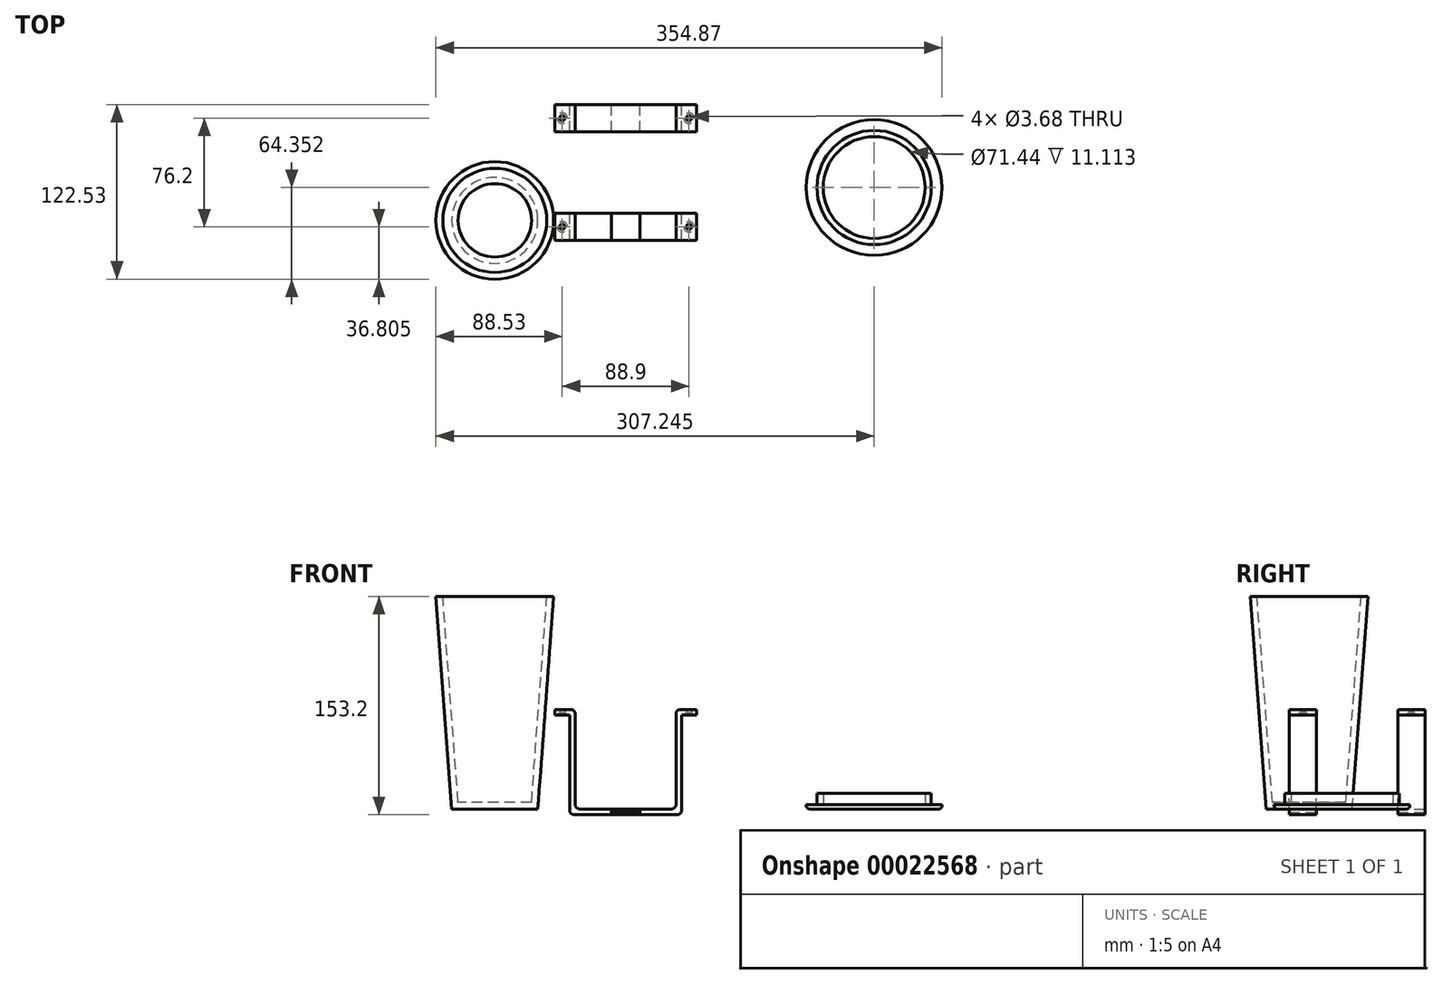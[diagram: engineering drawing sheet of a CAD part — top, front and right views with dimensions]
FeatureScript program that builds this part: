
annotation { "Feature Type Name" : "Feature", "Feature Type Description" : "" }
export const myFeature = defineFeature(function(context is Context, id is Id, definition is map)
    precondition{}
    {
        {
            var Q0;
            Q0=qCreatedBy(makeId("Front.planeOp"),FACE);
            var sketch = newSketch(context, id + "F0", { "sketchPlane" : qUnion([Q0])});
            skLineSegment(sketch, "E0", {"start": v(32.15, 0) * mm, "end": v(-32.15, 0) * mm});
            skLineSegment(sketch, "E1", {"start": v(35.32, 3.18) * mm, "end": v(35.32, 66.68) * mm});
            skLineSegment(sketch, "E2", {"start": v(-35.32, 3.18) * mm, "end": v(-35.32, 66.68) * mm});
            skLineSegment(sketch, "E3", {"start": v(-38.5, 69.85) * mm, "end": v(-49.6, 69.85) * mm});
            skLineSegment(sketch, "E4", {"start": v(38.5, 69.85) * mm, "end": v(49.6, 69.85) * mm});
            skLineSegment(sketch, "E5.0", {"start": v(39.3, 65.88) * mm, "end": v(49.6, 65.88) * mm});
            skLineSegment(sketch, "E5.1", {"start": v(-39.3, 65.88) * mm, "end": v(-49.6, 65.88) * mm});
            skLineSegment(sketch, "E5.2", {"start": v(-39.3, -0.8) * mm, "end": v(-39.3, 65.88) * mm});
            skLineSegment(sketch, "E5.3", {"start": v(36.12, -3.97) * mm, "end": v(-36.12, -3.97) * mm});
            skLineSegment(sketch, "E5.4", {"start": v(39.3, -0.8) * mm, "end": v(39.3, 65.88) * mm});
            skLineSegment(sketch, "E6", {"start": v(49.6, 69.85) * mm, "end": v(49.6, 65.88) * mm});
            skLineSegment(sketch, "E7", {"start": v(-49.6, 69.85) * mm, "end": v(-49.6, 65.88) * mm});
            skPoint(sketch, "E8.visualSharp", {"position": v(-35.32, 69.85) * mm});
            skArc(sketch, "E8.filletArc", {"start": v(-35.32, 66.68) * mm, "mid": v(-36.25, 68.92) * mm, "end": v(-38.5, 69.85) * mm});
            skPoint(sketch, "E9.visualSharp", {"position": v(-35.32, 0) * mm});
            skArc(sketch, "E9.filletArc", {"start": v(-35.32, 3.18) * mm, "mid": v(-34.4, 0.93) * mm, "end": v(-32.15, 0) * mm});
            skPoint(sketch, "E10.visualSharp", {"position": v(-39.3, -3.97) * mm});
            skArc(sketch, "E10.filletArc", {"start": v(-39.3, -0.8) * mm, "mid": v(-38.36, -3.04) * mm, "end": v(-36.12, -3.97) * mm});
            skPoint(sketch, "E11.visualSharp", {"position": v(39.3, -3.97) * mm});
            skArc(sketch, "E11.filletArc", {"start": v(36.12, -3.97) * mm, "mid": v(38.36, -3.04) * mm, "end": v(39.3, -0.8) * mm});
            skPoint(sketch, "E12.visualSharp", {"position": v(35.32, 0) * mm});
            skArc(sketch, "E12.filletArc", {"start": v(32.15, 0) * mm, "mid": v(34.4, 0.93) * mm, "end": v(35.32, 3.18) * mm});
            skPoint(sketch, "E13.visualSharp", {"position": v(35.32, 69.85) * mm});
            skArc(sketch, "E13.filletArc", {"start": v(38.5, 69.85) * mm, "mid": v(36.25, 68.92) * mm, "end": v(35.32, 66.68) * mm});
            skSolve(sketch);
        }
        {
            var Q0;
            Q0 = qSketchRegion(id + "F0", true);
            extrude(context, id + "F1", {"entities" : qUnion([Q0]), "depth" : 19.05 * mm});
        }
        {
            var Q0;
            Q0=makeQuery(id+"F1.opExtrude","SWEPT_BODY",BODY,{"disambiguationData":[OSD([sQuery(id+"F0.wireOp",EDGE,"E0"),sQuery(id+"F0.wireOp",EDGE,"E1"),sQuery(id+"F0.wireOp",EDGE,"E2"),sQuery(id+"F0.wireOp",EDGE,"E3"),sQuery(id+"F0.wireOp",EDGE,"E4"),sQuery(id+"F0.wireOp",EDGE,"E5.0"),sQuery(id+"F0.wireOp",EDGE,"E5.1"),sQuery(id+"F0.wireOp",EDGE,"E5.2"),sQuery(id+"F0.wireOp",EDGE,"E5.3"),sQuery(id+"F0.wireOp",EDGE,"E5.4"),sQuery(id+"F0.wireOp",EDGE,"E8.filletArc"),sQuery(id+"F0.wireOp",EDGE,"E9.filletArc"),sQuery(id+"F0.wireOp",EDGE,"E10.filletArc"),sQuery(id+"F0.wireOp",EDGE,"E11.filletArc"),sQuery(id+"F0.wireOp",EDGE,"E12.filletArc"),sQuery(id+"F0.wireOp",EDGE,"E13.filletArc"),sQuery(id+"F0.wireOp",EDGE,"E6"),sQuery(id+"F0.wireOp",EDGE,"E7")])]});
            transform(context, id + "F2", {"entities" : qUnion([Q0]), "transformType" : TransformType.TRANSLATION_3D, "dx" : 0 * mm, "dy" : 76.2 * mm, "dz" : 0 * mm, "makeCopy" : true});
        }
        {
            var Q0;
            Q0=makeQuery(id+"F1.opExtrude","CAP_FACE",FACE,{"disambiguationData":[OSD([sQuery(id+"F0.wireOp",EDGE,"E0"),sQuery(id+"F0.wireOp",EDGE,"E1"),sQuery(id+"F0.wireOp",EDGE,"E2"),sQuery(id+"F0.wireOp",EDGE,"E3"),sQuery(id+"F0.wireOp",EDGE,"E4"),sQuery(id+"F0.wireOp",EDGE,"E5.0"),sQuery(id+"F0.wireOp",EDGE,"E5.1"),sQuery(id+"F0.wireOp",EDGE,"E5.2"),sQuery(id+"F0.wireOp",EDGE,"E5.3"),sQuery(id+"F0.wireOp",EDGE,"E5.4"),sQuery(id+"F0.wireOp",EDGE,"E8.filletArc"),sQuery(id+"F0.wireOp",EDGE,"E9.filletArc"),sQuery(id+"F0.wireOp",EDGE,"E10.filletArc"),sQuery(id+"F0.wireOp",EDGE,"E11.filletArc"),sQuery(id+"F0.wireOp",EDGE,"E12.filletArc"),sQuery(id+"F0.wireOp",EDGE,"E13.filletArc"),sQuery(id+"F0.wireOp",EDGE,"E6"),sQuery(id+"F0.wireOp",EDGE,"E7")])],"isStart":false});
            var sketch = newSketch(context, id + "F3", { "sketchPlane" : qUnion([Q0])});
            skLineSegment(sketch, "E14", {"start": v(0, 0) * mm, "end": v(0, -3.97) * mm, "construction": true});
            skLineSegment(sketch, "E15.bottom", {"start": v(-9.92, 0) * mm, "end": v(0, 0) * mm});
            skLineSegment(sketch, "E15.top", {"start": v(-9.92, -2.5) * mm, "end": v(9.92, -2.5) * mm});
            skLineSegment(sketch, "E15.left", {"start": v(-9.92, 0) * mm, "end": v(-9.92, -2.5) * mm});
            skLineSegment(sketch, "E15.right", {"start": v(9.92, 0) * mm, "end": v(9.92, -2.5) * mm});
            skLineSegment(sketch, "E16", {"start": v(0, 0) * mm, "end": v(9.92, 0) * mm});
            skSolve(sketch);
        }
        {
            var Q0;
            Q0 = qSketchRegion(id + "F3", true);
            extrude(context, id + "F4", {"entities" : qUnion([Q0]), "operationType" : NewBodyOperationType.REMOVE, "endBound" : BoundingType.UP_TO_NEXT, "oppositeDirection" : true, "depth" : 25.4 * mm});
        }
        {
            var Q0;
            Q0=makeQuery(id+"F2.opPattern","COPY",FACE,{"derivedFrom":makeQuery(id+"F1.opExtrude","CAP_FACE",FACE,{"disambiguationData":[OSD([sQuery(id+"F0.wireOp",EDGE,"E0"),sQuery(id+"F0.wireOp",EDGE,"E1"),sQuery(id+"F0.wireOp",EDGE,"E2"),sQuery(id+"F0.wireOp",EDGE,"E3"),sQuery(id+"F0.wireOp",EDGE,"E4"),sQuery(id+"F0.wireOp",EDGE,"E5.0"),sQuery(id+"F0.wireOp",EDGE,"E5.1"),sQuery(id+"F0.wireOp",EDGE,"E5.2"),sQuery(id+"F0.wireOp",EDGE,"E5.3"),sQuery(id+"F0.wireOp",EDGE,"E5.4"),sQuery(id+"F0.wireOp",EDGE,"E8.filletArc"),sQuery(id+"F0.wireOp",EDGE,"E9.filletArc"),sQuery(id+"F0.wireOp",EDGE,"E10.filletArc"),sQuery(id+"F0.wireOp",EDGE,"E11.filletArc"),sQuery(id+"F0.wireOp",EDGE,"E12.filletArc"),sQuery(id+"F0.wireOp",EDGE,"E13.filletArc"),sQuery(id+"F0.wireOp",EDGE,"E6"),sQuery(id+"F0.wireOp",EDGE,"E7")])],"isStart":true}),"instanceName":"1"});
            var sketch = newSketch(context, id + "F5", { "sketchPlane" : qUnion([Q0])});
            skLineSegment(sketch, "E17", {"start": v(0, 0) * mm, "end": v(0, -3.97) * mm});
            skLineSegment(sketch, "E18.bottom", {"start": v(-9.92, -2.25) * mm, "end": v(9.92, -2.25) * mm});
            skLineSegment(sketch, "E18.top", {"start": v(-9.92, -3.97) * mm, "end": v(9.92, -3.97) * mm});
            skLineSegment(sketch, "E18.left", {"start": v(-9.92, -2.25) * mm, "end": v(-9.92, -3.97) * mm});
            skLineSegment(sketch, "E18.right", {"start": v(9.92, -2.25) * mm, "end": v(9.92, -3.97) * mm});
            skSolve(sketch);
        }
        {
            var Q0;
            Q0 = qSketchRegion(id + "F5", true);
            extrude(context, id + "F6", {"entities" : qUnion([Q0]), "operationType" : NewBodyOperationType.REMOVE, "endBound" : BoundingType.UP_TO_NEXT, "oppositeDirection" : true, "depth" : 25.4 * mm});
        }
        {
            var Q0;
            Q0=makeQuery(id+"F2.opPattern","COPY",FACE,{"derivedFrom":makeQuery(id+"F1.opExtrude","SWEPT_FACE",FACE,{"disambiguationData":[OSD([sQuery(id+"F0.wireOp",EDGE,"E5.0")])]}),"instanceName":"1"});
            var sketch = newSketch(context, id + "F7", { "sketchPlane" : qUnion([Q0])});
            skLineSegment(sketch, "E19", {"start": v(44.45, -76.2) * mm, "end": v(44.45, -57.15) * mm, "construction": true});
            skLineSegment(sketch, "E20", {"start": v(44.45, 0) * mm, "end": v(44.45, 19.05) * mm, "construction": true});
            skLineSegment(sketch, "E21", {"start": v(-44.45, 19.05) * mm, "end": v(-44.45, 0) * mm, "construction": true});
            skLineSegment(sketch, "E22", {"start": v(-44.45, -57.15) * mm, "end": v(-44.45, -76.2) * mm, "construction": true});
            skPoint(sketch, "E23", {"position": v(44.45, -66.68) * mm});
            skPoint(sketch, "E24", {"position": v(-44.45, -66.68) * mm});
            skPoint(sketch, "E25", {"position": v(-44.45, 9.53) * mm});
            skPoint(sketch, "E26", {"position": v(44.45, 9.53) * mm});
            skSolve(sketch);
        }
        {
            var Q0;
            Q0=sQuery(id+"F7.wireOp",VERTEX,"E23");
            var Q1;
            Q1=sQuery(id+"F7.wireOp",VERTEX,"E24");
            var Q2;
            Q2=sQuery(id+"F7.wireOp",VERTEX,"E25");
            var Q3;
            Q3=sQuery(id+"F7.wireOp",VERTEX,"E26");
            var Q4;
            Q4=makeQuery(id+"F2.opPattern","COPY",BODY,{"derivedFrom":makeQuery(id+"F1.opExtrude","SWEPT_BODY",BODY,{"disambiguationData":[OSD([sQuery(id+"F0.wireOp",EDGE,"E0"),sQuery(id+"F0.wireOp",EDGE,"E1"),sQuery(id+"F0.wireOp",EDGE,"E2"),sQuery(id+"F0.wireOp",EDGE,"E3"),sQuery(id+"F0.wireOp",EDGE,"E4"),sQuery(id+"F0.wireOp",EDGE,"E5.0"),sQuery(id+"F0.wireOp",EDGE,"E5.1"),sQuery(id+"F0.wireOp",EDGE,"E5.2"),sQuery(id+"F0.wireOp",EDGE,"E5.3"),sQuery(id+"F0.wireOp",EDGE,"E5.4"),sQuery(id+"F0.wireOp",EDGE,"E8.filletArc"),sQuery(id+"F0.wireOp",EDGE,"E9.filletArc"),sQuery(id+"F0.wireOp",EDGE,"E10.filletArc"),sQuery(id+"F0.wireOp",EDGE,"E11.filletArc"),sQuery(id+"F0.wireOp",EDGE,"E12.filletArc"),sQuery(id+"F0.wireOp",EDGE,"E13.filletArc"),sQuery(id+"F0.wireOp",EDGE,"E6"),sQuery(id+"F0.wireOp",EDGE,"E7")])]}),"instanceName":"1"});
            var Q5;
            Q5=makeQuery(id+"F1.opExtrude","SWEPT_BODY",BODY,{"disambiguationData":[OSD([sQuery(id+"F0.wireOp",EDGE,"E0"),sQuery(id+"F0.wireOp",EDGE,"E1"),sQuery(id+"F0.wireOp",EDGE,"E2"),sQuery(id+"F0.wireOp",EDGE,"E3"),sQuery(id+"F0.wireOp",EDGE,"E4"),sQuery(id+"F0.wireOp",EDGE,"E5.0"),sQuery(id+"F0.wireOp",EDGE,"E5.1"),sQuery(id+"F0.wireOp",EDGE,"E5.2"),sQuery(id+"F0.wireOp",EDGE,"E5.3"),sQuery(id+"F0.wireOp",EDGE,"E5.4"),sQuery(id+"F0.wireOp",EDGE,"E8.filletArc"),sQuery(id+"F0.wireOp",EDGE,"E9.filletArc"),sQuery(id+"F0.wireOp",EDGE,"E10.filletArc"),sQuery(id+"F0.wireOp",EDGE,"E11.filletArc"),sQuery(id+"F0.wireOp",EDGE,"E12.filletArc"),sQuery(id+"F0.wireOp",EDGE,"E13.filletArc"),sQuery(id+"F0.wireOp",EDGE,"E6"),sQuery(id+"F0.wireOp",EDGE,"E7")])]});
            hole(context, id + "F8", {"style" : HoleStyle.C_SINK, "holeDiameter" : 3.68 * mm, "cSinkDiameter" : 7.37 * mm, "endStyle" : HoleEndStyle.THROUGH, "locations" : qUnion([Q0, Q1, Q2, Q3]), "scope" : qUnion([Q4, Q5]), "cSinkAngle" : 90 * degree});
        }
        {
            var Q0;
            Q0=qCreatedBy(makeId("Top.planeOp"),FACE);
            var sketch = newSketch(context, id + "F9", { "sketchPlane" : qUnion([Q0])});
            skCircle(sketch, "E27", {"center": v(-91.7, -5.05) * mm, "radius": 30.16 * mm});
            skSolve(sketch);
        }
        {
            var Q0;
            Q0=qCreatedBy(makeId("Top.planeOp"),FACE);
            cPlane(context, id + "F10", {"entities" : qUnion([Q0]), "cplaneType" : CPlaneType.OFFSET, "offset" : 149.22 * mm, "width" : 152.4 * mm, "height" : 152.4 * mm});
        }
        {
            var Q0;
            Q0=qCreatedBy(id+"F10.planeOp",FACE);
            var sketch = newSketch(context, id + "F11", { "sketchPlane" : qUnion([Q0])});
            skCircle(sketch, "E28", {"center": v(-91.7, -5.05) * mm, "radius": 41.28 * mm});
            skSolve(sketch);
        }
        {
            var Q0;
            Q0=makeQuery(id+"F9.imprint","IMPRINT",FACE,{"disambiguationData":[TD([[makeQuery(id+"F9.imprint","IMPRINT",EDGE,{"derivedFrom":sQuery(id+"F9.wireOp",EDGE,"E27")}),1.0]])]});
            var Q1;
            Q1=makeQuery(id+"F11.imprint","IMPRINT",FACE,{"disambiguationData":[TD([[makeQuery(id+"F11.imprint","IMPRINT",EDGE,{"derivedFrom":sQuery(id+"F11.wireOp",EDGE,"E28")}),1.0]])]});
            loft(context, id + "F12", {"sheetProfilesArray" : [{ "sheetProfileEntities" : qUnion([Q0]) }, { "sheetProfileEntities" : qUnion([Q1]) }]});
        }
        {
            var Q0;
            Q0=makeQuery(id+"F12.opLoft","CAP_FACE",FACE,{"disambiguationData":[OSD([makeQuery(id+"F11.imprint","IMPRINT",FACE,{"disambiguationData":[TD([[makeQuery(id+"F11.imprint","IMPRINT",EDGE,{"derivedFrom":sQuery(id+"F11.wireOp",EDGE,"E28")}),1.0]])]})])],"isStart":true});
            shell(context, id + "F13", {"entities" : qUnion([Q0]), "thickness" : 4.76 * mm});
        }
        {
            var Q0;
            Q0=qCreatedBy(makeId("Top.planeOp"),FACE);
            var sketch = newSketch(context, id + "F14", { "sketchPlane" : qUnion([Q0])});
            skCircle(sketch, "E29", {"center": v(174.26, 18.02) * mm, "radius": 47.63 * mm});
            skCircle(sketch, "E30", {"center": v(174.26, 18.02) * mm, "radius": 35.72 * mm});
            skSolve(sketch);
        }
        {
            var Q0;
            Q0=makeQuery(id+"F14.imprint","IMPRINT",FACE,{"disambiguationData":[TD([[makeQuery(id+"F14.imprint","IMPRINT",EDGE,{"derivedFrom":sQuery(id+"F14.wireOp",EDGE,"E29")}),1.0]])]});
            extrude(context, id + "F15", {"entities" : qUnion([Q0]), "depth" : 3.17 * mm});
        }
        {
            var Q0;
            Q0=makeQuery(id+"F15.opExtrude","CAP_FACE",FACE,{"disambiguationData":[OSD([sQuery(id+"F14.wireOp",EDGE,"E29"),sQuery(id+"F14.wireOp",EDGE,"E30")])],"isStart":false});
            var sketch = newSketch(context, id + "F16", { "sketchPlane" : qUnion([Q0])});
            skCircle(sketch, "E31", {"center": v(174.26, 18.02) * mm, "radius": 35.72 * mm});
            skCircle(sketch, "E32", {"center": v(174.26, 18.02) * mm, "radius": 40.08 * mm});
            skSolve(sketch);
        }
        {
            var Q0;
            Q0=makeQuery(id+"F16.imprint","IMPRINT",FACE,{"disambiguationData":[TD([[makeQuery(id+"F16.imprint","IMPRINT",EDGE,{"derivedFrom":sQuery(id+"F16.wireOp",EDGE,"E31")}),-1.0]])]});
            extrude(context, id + "F17", {"entities" : qUnion([Q0]), "operationType" : NewBodyOperationType.ADD, "depth" : 7.94 * mm});
        }
        {
            var Q0;
            Q0=makeQuery(id+"F15.opExtrude","CAP_EDGE",EDGE,{"disambiguationData":[OSD([sQuery(id+"F14.wireOp",EDGE,"E29")])],"isStart":true});
            fillet(context, id + "F18", {"entities" : qUnion([Q0]), "radius" : 2.38 * mm, "tangentPropagation" : true, "allowEdgeOverflow" : false});
        }
    });
